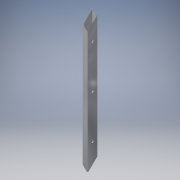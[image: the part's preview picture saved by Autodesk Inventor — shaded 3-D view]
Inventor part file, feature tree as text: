
AUTODESK INVENTOR PART (.ipt)
format: ipt  version: 2016 (Build 200138000, 138)  size: 134,656 bytes
history: native  units: in
note: dims shown in document units (in); Inventor stores cm internally (conversion verified against a paired STEP export)
features: extrude x2, sketch x2
ambient origin geometry x8: Origin, YZ Plane, XZ Plane, XY Plane, X Axis, Y Axis, Z Axis, Center Point
bodies: Solid1 (feature_tree)
feature tree (4):
  extrude  "Extrusion1"  Depth=2.0in
  extrude  "Extrusion2"  Depth=28.0in TaperAngle=0.0deg
  sketch  "Sketch1"  dims[d0=1.0in d1=2.0in]
  sketch  "Sketch2"  dims[d2=0.125in d3=28.0in d4=0.0in d5=0.5in d6=14.0in d7=1.0in d8=1.0in d9=0.0in d10=0.5in d11=1.5in d12=9.0in d13=0.5in d14=1.5in d15=9.0in]
